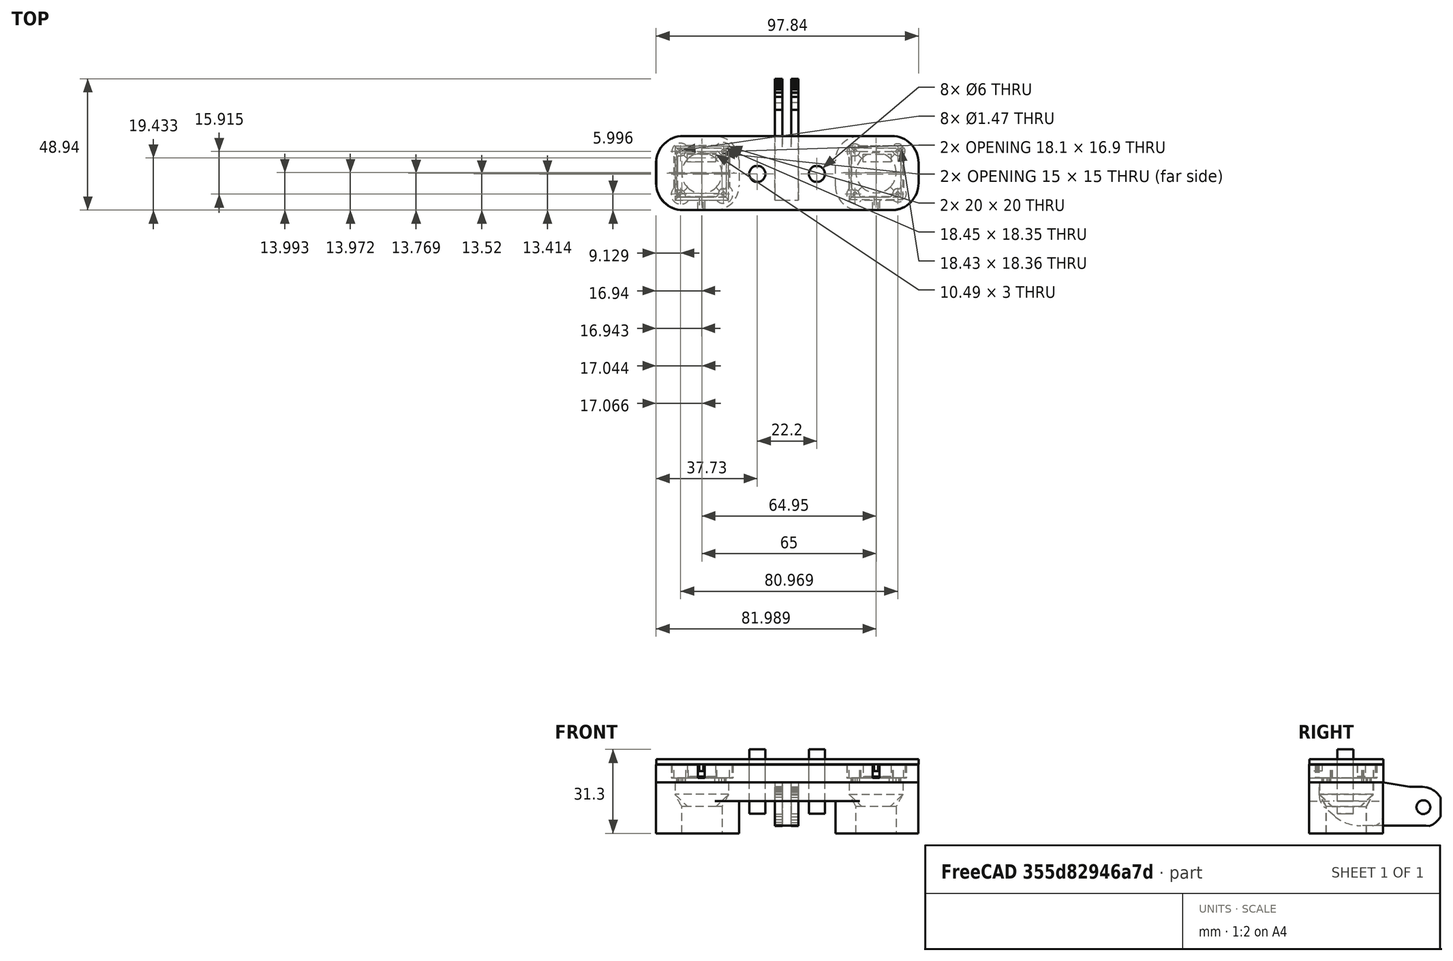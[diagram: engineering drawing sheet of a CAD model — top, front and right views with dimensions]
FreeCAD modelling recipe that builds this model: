
FCSTD DOCUMENT  (FreeCAD 0.19R24267 +99 (Git))
Label: 3D相机支架
License: All rights reserved
LicenseURL: http://en.wikipedia.org/wiki/All_rights_reserved
objects: Sketcher::SketchObject×15, PartDesign::Pad×11, Part::Cylinder×8, PartDesign::Fillet×7, App::Part×7, PartDesign::Body×6, Part::Cut×4, PartDesign::Pocket×3, PartDesign::ShapeBinder×2, Image::ImagePlane×1, PartDesign::Plane×1, PartDesign::AdditiveLoft×1, Mesh::Feature×1, Part::MultiFuse×1, App::MeasureDistance×1
note: 81 computed .brp shape members not serialized (recipe doc carries the construction recipe); baked Part::Feature solids carry a one-line shape summary decoded from their .brp

FEATURE [Image::ImagePlane] ImagePlane
  Placement = pos=(0.0706851,8.99972,0) rot=(0,0,-1;4.72024rad)
  XSize = 131.603
  YSize = 98.9214
FEATURE [Sketcher::SketchObject] Sketch
  FullyConstrained = false
  MapMode = 5
  Support = -> [XY_Plane]
  sketch-geometry (26):
    g0: LineSegment StartX=-2.6098 StartY=9.91969 StartZ=0 EndX=16.3902 EndY=9.91969 EndZ=0
    g1: LineSegment StartX=16.3902 StartY=9.91969 StartZ=0 EndX=16.3902 EndY=-9.08031 EndZ=0
    g2: LineSegment StartX=16.3902 StartY=-9.08031 StartZ=0 EndX=-2.6098 EndY=-9.08031 EndZ=0
    g3: LineSegment StartX=-2.6098 StartY=-9.08031 StartZ=0 EndX=-2.6098 EndY=9.91969 EndZ=0
    g4: Circle CenterX=-1.02434 CenterY=8.30105 CenterZ=0 NormalX=0 NormalY=0 NormalZ=1 AngleXU=0 Radius=0.734567
    g5: Circle CenterX=14.8836 CenterY=8.28387 CenterZ=0 NormalX=0 NormalY=0 NormalZ=1 AngleXU=0 Radius=0.734567
    g6: Circle CenterX=14.891 CenterY=-7.66127 CenterZ=0 NormalX=0 NormalY=0 NormalZ=1 AngleXU=0 Radius=0.734567
    g7: Circle CenterX=-0.958796 CenterY=-7.66815 CenterZ=0 NormalX=0 NormalY=0 NormalZ=1 AngleXU=0 Radius=0.734567
    g8: LineSegment StartX=0.44853 StartY=8.13558 StartZ=0 EndX=0.44853 EndY=8.77965 EndZ=0
    g9: ArcOfCircle CenterX=1.08417 CenterY=8.77965 CenterZ=0 NormalX=0 NormalY=0 NormalZ=1 AngleXU=0 Radius=0.63564 StartAngle=1.66062 EndAngle=3.14159
    g10: LineSegment StartX=1.02715 StartY=9.41273 StartZ=0 EndX=12.8411 EndY=9.41273 EndZ=0
    g11: ArcOfCircle CenterX=12.8411 CenterY=8.9738 CenterZ=0 NormalX=0 NormalY=0 NormalZ=1 AngleXU=0 Radius=0.43893 StartAngle=6.26572 EndAngle=7.85398
    g12: LineSegment StartX=13.2799 StartY=8.96613 StartZ=0 EndX=13.2799 EndY=8.11104 EndZ=0
    g13: ArcOfCircle CenterX=14.9168 CenterY=8.11104 CenterZ=0 NormalX=0 NormalY=0 NormalZ=1 AngleXU=0 Radius=1.63683 StartAngle=3.14159 EndAngle=4.6686
    g14: LineSegment StartX=14.8451 StartY=6.47577 StartZ=0 EndX=14.8451 EndY=-5.31443 EndZ=0
    g15: ArcOfCircle CenterX=14.0301 CenterY=-5.31443 CenterZ=0 NormalX=0 NormalY=0 NormalZ=1 AngleXU=0 Radius=0.815031 StartAngle=5.24992 EndAngle=6.28319
    g16: ArcOfCircle CenterX=15.6798 CenterY=-8.0821 CenterZ=0 NormalX=0 NormalY=0 NormalZ=1 AngleXU=0 Radius=2.40703 StartAngle=2.10833 EndAngle=3.12033
    g17: ArcOfCircle CenterX=12.6009 CenterY=-8.01664 CenterZ=0 NormalX=0 NormalY=0 NormalZ=1 AngleXU=0 Radius=0.67253 StartAngle=4.81773 EndAngle=6.26193
    g18: LineSegment StartX=12.6717 StartY=-8.68544 StartZ=0 EndX=1.5102 EndY=-8.68544 EndZ=0
    g19: ArcOfCircle CenterX=1.5102 CenterY=-8.10037 CenterZ=0 NormalX=0 NormalY=0 NormalZ=1 AngleXU=0 Radius=0.585068 StartAngle=3.0331 EndAngle=4.71239
    g20: LineSegment StartX=0.928577 StartY=-8.03702 StartZ=0 EndX=0.928577 EndY=-7.40934 EndZ=0
    g21: ArcOfCircle CenterX=-0.654332 CenterY=-7.40934 CenterZ=0 NormalX=0 NormalY=0 NormalZ=1 AngleXU=0 Radius=1.58291 StartAngle=0 EndAngle=1.58988
    g22: ArcOfCircle CenterX=-0.710267 CenterY=-4.47836 CenterZ=0 NormalX=0 NormalY=0 NormalZ=1 AngleXU=0 Radius=1.34861 StartAngle=3.18344 EndAngle=4.73147
    g23: LineSegment StartX=-2.0577 StartY=-4.53478 StartZ=0 EndX=-2.0577 EndY=5.76747 EndZ=0
    g24: ArcOfCircle CenterX=-1.11072 CenterY=5.76747 CenterZ=0 NormalX=0 NormalY=0 NormalZ=1 AngleXU=0 Radius=0.94698 StartAngle=1.54594 EndAngle=3.14159
    g25: ArcOfCircle CenterX=-1.0499 CenterY=8.21418 CenterZ=0 NormalX=0 NormalY=0 NormalZ=1 AngleXU=0 Radius=1.50049 StartAngle=4.68754 EndAngle=6.23078
  constraints (35):
    c: Coincident(g0,g1)
    c: Coincident(g1,g2)
    c: Coincident(g2,g3)
    c: Coincident(g3,g0)
    c: Horizontal(g0)
    c: Horizontal(g2)
    c: Vertical(g1)
    c: Vertical(g3)
    c: Distance(g0) = 19
    c: Equal(g3,g0)
    c: Vertical(g8)
    c: Tangent(g8,g9) = 1.5708
    c: Coincident(g9,g10)
    c: Horizontal(g10)
    c: Tangent(g10,g11) = 1.5708
    c: Coincident(g11,g12)
    c: Vertical(g12)
    c: Tangent(g12,g13) = -1.5708
    c: Coincident(g13,g14)
    c: Vertical(g14)
    c: Tangent(g14,g15) = 1.5708
    c: Tangent(g15,g16) = 1.5708
    c: Tangent(g16,g17) = 1.5708
    c: Coincident(g17,g18)
    c: Horizontal(g18)
    c: Tangent(g18,g19) = 1.5708
    c: Coincident(g19,g20)
    c: Vertical(g20)
    c: Tangent(g20,g21) = -1.5708
    c: Tangent(g21,g22) = 1.5708
    c: Coincident(g22,g23)
    c: Vertical(g23)
    c: Tangent(g23,g24) = 1.5708
    c: Tangent(g24,g25) = 1.5708
    c: Coincident(g25,g8)
FEATURE [PartDesign::Pad] Pad
  Direction = (1,1,1)
  Length = 1.6
  Length2 = 100
  Profile = -> Sketch
  Type = 0
FEATURE [PartDesign::Body] Body
  Group = -> [Sketch,Pad]
  Origin = -> Origin
  Placement = pos=(0,0,0) rot=(0,0,1;1.5708rad)
  Tip = -> Pad
FEATURE [Sketcher::SketchObject] Sketch001
  FullyConstrained = false
  MapMode = 5
  Support = -> [XY_Plane001]
  sketch-geometry (26):
    g0: LineSegment StartX=-2.6098 StartY=9.91969 StartZ=0 EndX=16.3902 EndY=9.91969 EndZ=0
    g1: LineSegment StartX=16.3902 StartY=9.91969 StartZ=0 EndX=16.3902 EndY=-9.08031 EndZ=0
    g2: LineSegment StartX=16.3902 StartY=-9.08031 StartZ=0 EndX=-2.6098 EndY=-9.08031 EndZ=0
    g3: LineSegment StartX=-2.6098 StartY=-9.08031 StartZ=0 EndX=-2.6098 EndY=9.91969 EndZ=0
    g4: Circle CenterX=-1.02434 CenterY=8.30105 CenterZ=0 NormalX=0 NormalY=0 NormalZ=1 AngleXU=0 Radius=0.734567
    g5: Circle CenterX=14.8836 CenterY=8.28387 CenterZ=0 NormalX=0 NormalY=0 NormalZ=1 AngleXU=0 Radius=0.734567
    g6: Circle CenterX=14.891 CenterY=-7.66127 CenterZ=0 NormalX=0 NormalY=0 NormalZ=1 AngleXU=0 Radius=0.734567
    g7: Circle CenterX=-0.958796 CenterY=-7.66815 CenterZ=0 NormalX=0 NormalY=0 NormalZ=1 AngleXU=0 Radius=0.734567
    g8: LineSegment StartX=0.44853 StartY=8.13558 StartZ=0 EndX=0.44853 EndY=8.77965 EndZ=0
    g9: ArcOfCircle CenterX=1.08417 CenterY=8.77965 CenterZ=0 NormalX=0 NormalY=0 NormalZ=1 AngleXU=0 Radius=0.63564 StartAngle=1.66062 EndAngle=3.14159
    g10: LineSegment StartX=1.02715 StartY=9.41273 StartZ=0 EndX=12.8411 EndY=9.41273 EndZ=0
    g11: ArcOfCircle CenterX=12.8411 CenterY=8.9738 CenterZ=0 NormalX=0 NormalY=0 NormalZ=1 AngleXU=0 Radius=0.43893 StartAngle=6.26572 EndAngle=7.85398
    g12: LineSegment StartX=13.2799 StartY=8.96613 StartZ=0 EndX=13.2799 EndY=8.11104 EndZ=0
    g13: ArcOfCircle CenterX=14.9168 CenterY=8.11104 CenterZ=0 NormalX=0 NormalY=0 NormalZ=1 AngleXU=0 Radius=1.63683 StartAngle=3.14159 EndAngle=4.6686
    g14: LineSegment StartX=14.8451 StartY=6.47577 StartZ=0 EndX=14.8451 EndY=-5.31443 EndZ=0
    g15: ArcOfCircle CenterX=14.0301 CenterY=-5.31443 CenterZ=0 NormalX=0 NormalY=0 NormalZ=1 AngleXU=0 Radius=0.815031 StartAngle=5.24992 EndAngle=6.28319
    g16: ArcOfCircle CenterX=15.6798 CenterY=-8.0821 CenterZ=0 NormalX=0 NormalY=0 NormalZ=1 AngleXU=0 Radius=2.40703 StartAngle=2.10833 EndAngle=3.12033
    g17: ArcOfCircle CenterX=12.6009 CenterY=-8.01664 CenterZ=0 NormalX=0 NormalY=0 NormalZ=1 AngleXU=0 Radius=0.67253 StartAngle=4.81773 EndAngle=6.26193
    g18: LineSegment StartX=12.6717 StartY=-8.68544 StartZ=0 EndX=1.5102 EndY=-8.68544 EndZ=0
    g19: ArcOfCircle CenterX=1.5102 CenterY=-8.10037 CenterZ=0 NormalX=0 NormalY=0 NormalZ=1 AngleXU=0 Radius=0.585068 StartAngle=3.0331 EndAngle=4.71239
    g20: LineSegment StartX=0.928577 StartY=-8.03702 StartZ=0 EndX=0.928577 EndY=-7.40934 EndZ=0
    g21: ArcOfCircle CenterX=-0.654332 CenterY=-7.40934 CenterZ=0 NormalX=0 NormalY=0 NormalZ=1 AngleXU=0 Radius=1.58291 StartAngle=0 EndAngle=1.58988
    g22: ArcOfCircle CenterX=-0.710267 CenterY=-4.47836 CenterZ=0 NormalX=0 NormalY=0 NormalZ=1 AngleXU=0 Radius=1.34861 StartAngle=3.18344 EndAngle=4.73147
    g23: LineSegment StartX=-2.0577 StartY=-4.53478 StartZ=0 EndX=-2.0577 EndY=5.76747 EndZ=0
    g24: ArcOfCircle CenterX=-1.11072 CenterY=5.76747 CenterZ=0 NormalX=0 NormalY=0 NormalZ=1 AngleXU=0 Radius=0.94698 StartAngle=1.54594 EndAngle=3.14159
    g25: ArcOfCircle CenterX=-1.0499 CenterY=8.21418 CenterZ=0 NormalX=0 NormalY=0 NormalZ=1 AngleXU=0 Radius=1.50049 StartAngle=4.68754 EndAngle=6.23078
  constraints (35):
    c: Coincident(g0,g1)
    c: Coincident(g1,g2)
    c: Coincident(g2,g3)
    c: Coincident(g3,g0)
    c: Horizontal(g0)
    c: Horizontal(g2)
    c: Vertical(g1)
    c: Vertical(g3)
    c: Distance(g0) = 19
    c: Equal(g3,g0)
    c: Vertical(g8)
    c: Tangent(g8,g9) = 1.5708
    c: Coincident(g9,g10)
    c: Horizontal(g10)
    c: Tangent(g10,g11) = 1.5708
    c: Coincident(g11,g12)
    c: Vertical(g12)
    c: Tangent(g12,g13) = -1.5708
    c: Coincident(g13,g14)
    c: Vertical(g14)
    c: Tangent(g14,g15) = 1.5708
    c: Tangent(g15,g16) = 1.5708
    c: Tangent(g16,g17) = 1.5708
    c: Coincident(g17,g18)
    c: Horizontal(g18)
    c: Tangent(g18,g19) = 1.5708
    c: Coincident(g19,g20)
    c: Vertical(g20)
    c: Tangent(g20,g21) = -1.5708
    c: Tangent(g21,g22) = 1.5708
    c: Coincident(g22,g23)
    c: Vertical(g23)
    c: Tangent(g23,g24) = 1.5708
    c: Tangent(g24,g25) = 1.5708
    c: Coincident(g25,g8)
FEATURE [PartDesign::Pad] Pad001
  Direction = (1,1,1)
  Length = 1.6
  Length2 = 100
  Profile = -> Sketch001
  Type = 0
FEATURE [PartDesign::Body] Body001
  Group = -> [Sketch001,Pad001]
  Origin = -> Origin001
  Placement = pos=(65,-1.4e-14,0) rot=(0,0,1;1.5708rad)
  Tip = -> Pad001
FEATURE [Sketcher::SketchObject] Sketch002
  FullyConstrained = false
  MapMode = 5
  Support = -> [XY_Plane002]
  sketch-geometry (12):
    g0: LineSegment StartX=-17.432 StartY=20.571 StartZ=0 EndX=80.3236 EndY=20.571 EndZ=0
    g1: LineSegment StartX=80.3236 StartY=20.571 StartZ=0 EndX=80.3236 EndY=-7.01778 EndZ=0
    g2: LineSegment StartX=80.3236 StartY=-7.01778 StartZ=0 EndX=-17.432 EndY=-7.01778 EndZ=0
    g3: LineSegment StartX=-17.432 StartY=-7.01778 StartZ=0 EndX=-17.432 EndY=20.571 EndZ=0
    g4: LineSegment StartX=-9.71325 StartY=16.1288 StartZ=0 EndX=8.73847 EndY=16.1288 EndZ=0
    g5: LineSegment StartX=8.73847 StartY=16.1288 StartZ=0 EndX=8.73847 EndY=-2.22466 EndZ=0
    g6: LineSegment StartX=8.73847 StartY=-2.22466 StartZ=0 EndX=-9.71325 EndY=-2.22466 EndZ=0
    g7: LineSegment StartX=-9.71325 StartY=-2.22466 StartZ=0 EndX=-9.71325 EndY=16.1288 EndZ=0
    g8: LineSegment StartX=55.3452 StartY=16.1523 StartZ=0 EndX=73.7733 EndY=16.1523 EndZ=0
    g9: LineSegment StartX=73.7733 StartY=16.1523 StartZ=0 EndX=73.7733 EndY=-2.20537 EndZ=0
    g10: LineSegment StartX=73.7733 StartY=-2.20537 StartZ=0 EndX=55.3452 EndY=-2.20537 EndZ=0
    g11: LineSegment StartX=55.3452 StartY=-2.20537 StartZ=0 EndX=55.3452 EndY=16.1523 EndZ=0
  constraints (24):
    c: Coincident(g0,g1)
    c: Coincident(g1,g2)
    c: Coincident(g2,g3)
    c: Coincident(g3,g0)
    c: Horizontal(g0)
    c: Horizontal(g2)
    c: Vertical(g1)
    c: Vertical(g3)
    c: Coincident(g4,g5)
    c: Coincident(g5,g6)
    c: Coincident(g6,g7)
    c: Coincident(g7,g4)
    c: Horizontal(g4)
    c: Horizontal(g6)
    c: Vertical(g5)
    c: Vertical(g7)
    c: Coincident(g8,g9)
    c: Coincident(g9,g10)
    c: Coincident(g10,g11)
    c: Coincident(g11,g8)
    c: Horizontal(g8)
    c: Horizontal(g10)
    c: Vertical(g9)
    c: Vertical(g11)
FEATURE [PartDesign::Pad] Pad002
  Direction = (1,1,1)
  Length = 1.6
  Length2 = 100
  Profile = -> Sketch002
  Type = 0
FEATURE [Sketcher::SketchObject] Sketch003
  ExternalGeometry = -> [Pad002]
  FullyConstrained = false
  MapMode = 5
  Placement = pos=(0,0,1.6) rot=(0,0,1;0rad)
  Support = -> [Pad002]
  sketch-geometry (20):
    g0: ArcOfCircle CenterX=-8.39912 CenterY=14.8619 CenterZ=0 NormalX=0 NormalY=0 NormalZ=1 AngleXU=0 Radius=3.11861 StartAngle=0.810898 EndAngle=3.8862
    g1: LineSegment StartX=-6.25088 StartY=17.1226 StartZ=0 EndX=5.01763 EndY=17.1226 EndZ=0
    g2: ArcOfCircle CenterX=7.48864 CenterY=14.9182 CenterZ=0 NormalX=0 NormalY=0 NormalZ=1 AngleXU=0 Radius=3.31135 StartAngle=5.53813 EndAngle=8.69636
    g3: LineSegment StartX=9.92265 StartY=12.6731 StartZ=0 EndX=9.92265 EndY=1.73188 EndZ=0
    g4: ArcOfCircle CenterX=7.71 CenterY=-0.982007 CenterZ=0 NormalX=0 NormalY=0 NormalZ=1 AngleXU=0 Radius=3.50157 StartAngle=3.92905 EndAngle=7.16998
    g5: LineSegment StartX=5.23912 StartY=-3.46308 StartZ=0 EndX=-5.40416 EndY=-3.46308 EndZ=0
    g6: ArcOfCircle CenterX=-8.20355 CenterY=-1.21839 CenterZ=0 NormalX=0 NormalY=0 NormalZ=1 AngleXU=0 Radius=3.58821 StartAngle=2.33729 EndAngle=5.60732
    g7: LineSegment StartX=-10.6924 StartY=1.36635 StartZ=0 EndX=-10.6924 EndY=12.7484 EndZ=0
    g8: ArcOfCircle CenterX=56.645 CenterY=14.753 CenterZ=0 NormalX=0 NormalY=0 NormalZ=1 AngleXU=0 Radius=2.88595 StartAngle=0.890269 EndAngle=3.86492
    g9: LineSegment StartX=58.4608 StartY=16.9961 StartZ=0 EndX=70.8307 EndY=16.9961 EndZ=0
    g10: ArcOfCircle CenterX=72.6637 CenterY=15.0338 CenterZ=0 NormalX=0 NormalY=0 NormalZ=1 AngleXU=0 Radius=2.68524 StartAngle=5.63874 EndAngle=8.60532
    g11: LineSegment StartX=74.8104 StartY=13.4206 StartZ=0 EndX=74.8104 EndY=1.34255 EndZ=0
    g12: ArcOfCircle CenterX=72.8298 CenterY=-0.933697 CenterZ=0 NormalX=0 NormalY=0 NormalZ=1 AngleXU=0 Radius=3.01727 StartAngle=4.08071 EndAngle=7.13793
    g13: LineSegment StartX=71.0481 StartY=-3.36875 StartZ=0 EndX=59.032 EndY=-3.36875 EndZ=0
    g14: ArcOfCircle CenterX=56.7248 CenterY=-1.25151 CenterZ=0 NormalX=0 NormalY=0 NormalZ=1 AngleXU=0 Radius=3.13143 StartAngle=2.36935 EndAngle=5.54069
    g15: LineSegment StartX=54.4816 StartY=0.933413 StartZ=0 EndX=54.4816 EndY=12.8429 EndZ=0
    g16: LineSegment StartX=-17.432 StartY=20.571 StartZ=0 EndX=80.3236 EndY=20.571 EndZ=0
    g17: LineSegment StartX=80.3236 StartY=20.571 StartZ=0 EndX=80.3236 EndY=-7.01778 EndZ=0
    g18: LineSegment StartX=80.3236 StartY=-7.01778 StartZ=0 EndX=-17.432 EndY=-7.01778 EndZ=0
    g19: LineSegment StartX=-17.432 StartY=-7.01778 StartZ=0 EndX=-17.432 EndY=20.571 EndZ=0
  constraints (34):
    c: Coincident(g0,g1)
    c: Horizontal(g1)
    c: Coincident(g2,g3)
    c: Coincident(g4,g5)
    c: Horizontal(g5)
    c: Coincident(g6,g7)
    c: Vertical(g7)
    c: Coincident(g7,g0)
    c: Coincident(g2,g1)
    c: Vertical(g3)
    c: Coincident(g4,g3)
    c: Coincident(g5,g6)
    c: Coincident(g8,g9)
    c: Horizontal(g9)
    c: Coincident(g10,g11)
    c: Coincident(g12,g13)
    c: Horizontal(g13)
    c: Coincident(g14,g15)
    c: Vertical(g15)
    c: Coincident(g15,g8)
    c: Coincident(g10,g9)
    c: Vertical(g11)
    c: Coincident(g12,g11)
    c: Coincident(g13,g14)
    c: Coincident(g16,g17)
    c: Coincident(g17,g18)
    c: Coincident(g18,g19)
    c: Coincident(g19,g16)
    c: Horizontal(g16)
    c: Horizontal(g18)
    c: Vertical(g17)
    c: Vertical(g19)
    c: Coincident(g16,g-5)
    c: Coincident(g17,g-6)
FEATURE [PartDesign::Pad] Pad003
  BaseFeature = -> Pad002
  Direction = (1,1,1)
  Length = 5
  Length2 = 100
  Profile = -> Sketch003
  Type = 0
FEATURE [PartDesign::ShapeBinder] CopyPad003
  TraceSupport = false
FEATURE [Sketcher::SketchObject] Sketch004
  FullyConstrained = false
  MapMode = 5
  Placement = pos=(0,0,0) rot=(1,0,0;3.14159rad)
  Support = -> [CopyPad003]
  sketch-geometry (12):
    g0: LineSegment StartX=-10.3859 StartY=3.2507 StartZ=0 EndX=9.61406 EndY=3.2507 EndZ=0
    g1: LineSegment StartX=9.61406 StartY=3.2507 StartZ=0 EndX=9.61406 EndY=-16.7493 EndZ=0
    g2: LineSegment StartX=9.61406 StartY=-16.7493 StartZ=0 EndX=-10.3859 EndY=-16.7493 EndZ=0
    g3: LineSegment StartX=-10.3859 StartY=-16.7493 StartZ=0 EndX=-10.3859 EndY=3.2507 EndZ=0
    g4: LineSegment StartX=74.5643 StartY=3.08146 StartZ=0 EndX=74.5643 EndY=-16.9185 EndZ=0
    g5: LineSegment StartX=54.5643 StartY=3.08146 StartZ=0 EndX=74.5643 EndY=3.08146 EndZ=0
    g6: LineSegment StartX=74.5643 StartY=-16.9185 StartZ=0 EndX=54.5643 EndY=-16.9185 EndZ=0
    g7: LineSegment StartX=54.5643 StartY=-16.9185 StartZ=0 EndX=54.5643 EndY=3.08146 EndZ=0
    g8: LineSegment StartX=-17.4318 StartY=7.01779 StartZ=0 EndX=80.319 EndY=7.01779 EndZ=0
    g9: LineSegment StartX=80.319 StartY=7.01779 StartZ=0 EndX=80.319 EndY=-20.5415 EndZ=0
    g10: LineSegment StartX=80.319 StartY=-20.5415 StartZ=0 EndX=-17.4318 EndY=-20.5415 EndZ=0
    g11: LineSegment StartX=-17.4318 StartY=-20.5415 StartZ=0 EndX=-17.4318 EndY=7.01779 EndZ=0
  constraints (28):
    c: Coincident(g0,g1)
    c: Coincident(g1,g2)
    c: Coincident(g2,g3)
    c: Coincident(g3,g0)
    c: Horizontal(g0)
    c: Horizontal(g2)
    c: Vertical(g1)
    c: Vertical(g3)
    c: Equal(g0,g3)
    c: Distance(g0) = 20
    c: Coincident(g5,g4)
    c: Coincident(g4,g6)
    c: Coincident(g6,g7)
    c: Coincident(g7,g5)
    c: Horizontal(g5)
    c: Horizontal(g6)
    c: Vertical(g4)
    c: Vertical(g7)
    c: Equal(g5,g7)
    c: Equal(g0,g5) = 20
    c: Coincident(g8,g9)
    c: Coincident(g9,g10)
    c: Coincident(g10,g11)
    c: Coincident(g11,g8)
    c: Horizontal(g8)
    c: Horizontal(g10)
    c: Vertical(g9)
    c: Vertical(g11)
FEATURE [PartDesign::Pad] Pad004
  Direction = (1,1,1)
  Length = 4.5
  Length2 = 100
  Profile = -> Sketch004
  Type = 0
FEATURE [Sketcher::SketchObject] Sketch005
  ExternalGeometry = -> [Pad004]
  FullyConstrained = true
  MapMode = 5
  Placement = pos=(0,0,-4.5) rot=(1,0,0;3.14159rad)
  Support = -> [Pad004]
  sketch-geometry (12):
    g0: LineSegment StartX=-17.4318 StartY=7.01779 StartZ=0 EndX=80.319 EndY=7.01779 EndZ=0
    g1: LineSegment StartX=80.319 StartY=7.01779 StartZ=0 EndX=80.319 EndY=-20.5415 EndZ=0
    g2: LineSegment StartX=80.319 StartY=-20.5415 StartZ=0 EndX=-17.4318 EndY=-20.5415 EndZ=0
    g3: LineSegment StartX=-17.4318 StartY=-20.5415 StartZ=0 EndX=-17.4318 EndY=7.01779 EndZ=0
    g4: LineSegment StartX=-10.3859 StartY=3.2507 StartZ=0 EndX=9.61406 EndY=3.2507 EndZ=0
    g5: LineSegment StartX=9.61406 StartY=3.2507 StartZ=0 EndX=9.61406 EndY=-16.7493 EndZ=0
    g6: LineSegment StartX=9.61406 StartY=-16.7493 StartZ=0 EndX=-10.3859 EndY=-16.7493 EndZ=0
    g7: LineSegment StartX=-10.3859 StartY=-16.7493 StartZ=0 EndX=-10.3859 EndY=3.2507 EndZ=0
    g8: LineSegment StartX=54.5643 StartY=3.08146 StartZ=0 EndX=74.5643 EndY=3.08146 EndZ=0
    g9: LineSegment StartX=74.5643 StartY=3.08146 StartZ=0 EndX=74.5643 EndY=-16.9185 EndZ=0
    g10: LineSegment StartX=74.5643 StartY=-16.9185 StartZ=0 EndX=54.5643 EndY=-16.9185 EndZ=0
    g11: LineSegment StartX=54.5643 StartY=-16.9185 StartZ=0 EndX=54.5643 EndY=3.08146 EndZ=0
  constraints (30):
    c: Coincident(g0,g1)
    c: Coincident(g1,g2)
    c: Coincident(g2,g3)
    c: Coincident(g3,g0)
    c: Horizontal(g0)
    c: Horizontal(g2)
    c: Vertical(g1)
    c: Vertical(g3)
    c: Coincident(g0,g-3)
    c: Coincident(g1,g-4)
    c: Coincident(g4,g5)
    c: Coincident(g5,g6)
    c: Coincident(g6,g7)
    c: Coincident(g7,g4)
    c: Horizontal(g4)
    c: Horizontal(g6)
    c: Vertical(g5)
    c: Vertical(g7)
    c: Coincident(g4,g-8)
    c: Coincident(g5,g-5)
    c: Coincident(g8,g9)
    c: Coincident(g9,g10)
    c: Coincident(g10,g11)
    c: Coincident(g11,g8)
    c: Horizontal(g8)
    c: Horizontal(g10)
    c: Vertical(g9)
    c: Vertical(g11)
    c: Coincident(g8,g-6)
    c: Coincident(g9,g-7)
FEATURE [PartDesign::ShapeBinder] CopyXY_Plane004
  TraceSupport = false
FEATURE [PartDesign::Plane] DatumPlane
  AttachmentOffset = pos=(0,0,-9) rot=(0,0,1;0rad)
  Length = 119.832
  MapMode = 5
  Placement = pos=(0,0,-9) rot=(0,0,1;0rad)
  ResizeMode = 0
  Support = -> [CopyXY_Plane004]
  Width = 64.5134
FEATURE [Sketcher::SketchObject] Sketch006
  ExternalGeometry = -> [Sketch005]
  FullyConstrained = true
  MapMode = 5
  Placement = pos=(0,0,-9) rot=(0,0,1;0rad)
  Support = -> [DatumPlane]
  sketch-geometry (12):
    g0: LineSegment StartX=-17.4318 StartY=20.5415 StartZ=0 EndX=80.319 EndY=20.5415 EndZ=0
    g1: LineSegment StartX=80.319 StartY=20.5415 StartZ=0 EndX=80.319 EndY=-7.01779 EndZ=0
    g2: LineSegment StartX=80.319 StartY=-7.01779 StartZ=0 EndX=-17.4318 EndY=-7.01779 EndZ=0
    g3: LineSegment StartX=-17.4318 StartY=-7.01779 StartZ=0 EndX=-17.4318 EndY=20.5415 EndZ=0
    g4: LineSegment StartX=-10.3859 StartY=16.7493 StartZ=0 EndX=9.61406 EndY=-3.2507 EndZ=0
    g5: LineSegment StartX=9.61406 StartY=16.7493 StartZ=0 EndX=-10.3859 EndY=-3.2507 EndZ=0
    g6: GeomPoint X=-0.385936 Y=6.7493 Z=0
    g7: LineSegment StartX=54.5643 StartY=16.9185 StartZ=0 EndX=74.5643 EndY=-3.08146 EndZ=0
    g8: LineSegment StartX=74.5643 StartY=16.9185 StartZ=0 EndX=54.5643 EndY=-3.08146 EndZ=0
    g9: GeomPoint X=64.5643 Y=6.91854 Z=0
    g10: Circle CenterX=-0.385936 CenterY=6.7493 CenterZ=0 NormalX=0 NormalY=0 NormalZ=1 AngleXU=0 Radius=7.5
    g11: Circle CenterX=64.5643 CenterY=6.91854 CenterZ=0 NormalX=0 NormalY=0 NormalZ=1 AngleXU=0 Radius=7.5
  constraints (26):
    c: Coincident(g0,g1)
    c: Coincident(g1,g2)
    c: Coincident(g2,g3)
    c: Coincident(g3,g0)
    c: Horizontal(g0)
    c: Horizontal(g2)
    c: Vertical(g1)
    c: Vertical(g3)
    c: Coincident(g-7,g0)
    c: Coincident(g1,g-8)
    c: Coincident(g4,g-3)
    c: Coincident(g4,g-5)
    c: Coincident(g5,g-3)
    c: Coincident(g5,g-5)
    c: PointOnObject(g6,g5)
    c: PointOnObject(g6,g4)
    c: Coincident(g7,g-4)
    c: Coincident(g7,g-6)
    c: Coincident(g8,g-4)
    c: Coincident(g8,g-6)
    c: PointOnObject(g9,g8)
    c: PointOnObject(g9,g7)
    c: Coincident(g10,g6)
    c: Diameter(g10) = 15
    c: Coincident(g11,g9)
    c: Diameter(g11) = 15
FEATURE [PartDesign::AdditiveLoft] AdditiveLoft
  BaseFeature = -> Pad004
  Closed = false
  Profile = -> Sketch005
  Ruled = false
  Sections = -> [Sketch006]
FEATURE [PartDesign::Pad] Pad005
  BaseFeature = -> AdditiveLoft
  Direction = (1,1,1)
  Length = 10
  Length2 = 100
  Profile = -> AdditiveLoft [Face17]
  Type = 0
FEATURE [PartDesign::Fillet] Fillet
  Base = -> Pad005 [Edge50,Edge47,Edge46,Edge52]
  BaseFeature = -> Pad005
  Radius = 10
  SupportTransform = false
FEATURE [Sketcher::SketchObject] Sketch007
  ExternalGeometry = -> [Fillet]
  FullyConstrained = false
  MapMode = 5
  Placement = pos=(0,0,-19) rot=(1,0,0;3.14159rad)
  Support = -> [Fillet]
  sketch-geometry (6):
    g0: LineSegment StartX=13.4592 StartY=8.86174 StartZ=0 EndX=49.428 EndY=8.86174 EndZ=0
    g1: LineSegment StartX=49.428 StartY=8.86174 StartZ=0 EndX=49.428 EndY=-27.2773 EndZ=0
    g2: LineSegment StartX=49.428 StartY=-27.2773 StartZ=0 EndX=13.4592 EndY=-27.2773 EndZ=0
    g3: LineSegment StartX=13.4592 StartY=-27.2773 StartZ=0 EndX=13.4592 EndY=8.86174 EndZ=0
    g4: LineSegment StartX=-17.4318 StartY=-2.98221 StartZ=0 EndX=13.4592 EndY=-2.98221 EndZ=0
    g5: LineSegment StartX=49.428 StartY=-2.98221 StartZ=0 EndX=80.319 EndY=-2.98221 EndZ=0
  constraints (15):
    c: Coincident(g0,g1)
    c: Coincident(g1,g2)
    c: Coincident(g2,g3)
    c: Coincident(g3,g0)
    c: Horizontal(g0)
    c: Horizontal(g2)
    c: Vertical(g1)
    c: Vertical(g3)
    c: Coincident(g4,g-3)
    c: PointOnObject(g4,g3)
    c: Horizontal(g4)
    c: PointOnObject(g5,g1)
    c: Coincident(g5,g-4)
    c: Horizontal(g5)
    c: Equal(g4,g5)
FEATURE [PartDesign::Pocket] Pocket
  BaseFeature = -> Fillet
  Length = 12
  Length2 = 100
  Profile = -> Sketch007
  Type = 0
FEATURE [PartDesign::Fillet] Fillet001
  Base = -> Pocket [Edge72,Edge68,Edge64,Edge74]
  BaseFeature = -> Pocket
  Radius = 9
  SupportTransform = false
FEATURE [PartDesign::Body] Body003
  Group = -> [CopyPad003,Sketch004,Pad004,Sketch005,DatumPlane,CopyXY_Plane004,Sketch006,AdditiveLoft,Pad005,Fillet,Sketch007,Pocket,Fillet001]
  Origin = -> Origin005
  Tip = -> Fillet001
FEATURE [App::Part] Part001  label="相机前框"
  Group = -> [Body003]
  Origin = -> Origin004
FEATURE [PartDesign::Fillet] Fillet002
  Base = -> Pad003 [Edge21,Edge26,Edge24,Edge20]
  BaseFeature = -> Pad003
  Radius = 10
  SupportTransform = false
FEATURE [Sketcher::SketchObject] Sketch008
  FullyConstrained = false
  MapMode = 5
  Placement = pos=(0,0,6.6) rot=(0,0,1;0rad)
  Support = -> [Fillet002]
  sketch-geometry (8):
    g0: LineSegment StartX=-1.83309 StartY=0.606132 StartZ=0 EndX=0.666909 EndY=0.606132 EndZ=0
    g1: LineSegment StartX=0.666909 StartY=0.606132 StartZ=0 EndX=0.666909 EndY=-8.63685 EndZ=0
    g2: LineSegment StartX=0.666909 StartY=-8.63685 StartZ=0 EndX=-1.83309 EndY=-8.63685 EndZ=0
    g3: LineSegment StartX=-1.83309 StartY=-8.63685 StartZ=0 EndX=-1.83309 EndY=0.606132 EndZ=0
    g4: LineSegment StartX=63.2717 StartY=0.846198 StartZ=0 EndX=65.7717 EndY=0.846198 EndZ=0
    g5: LineSegment StartX=65.7717 StartY=0.846198 StartZ=0 EndX=65.7717 EndY=-9.55029 EndZ=0
    g6: LineSegment StartX=65.7717 StartY=-9.55029 StartZ=0 EndX=63.2717 EndY=-9.55029 EndZ=0
    g7: LineSegment StartX=63.2717 StartY=-9.55029 StartZ=0 EndX=63.2717 EndY=0.846198 EndZ=0
  constraints (18):
    c: Coincident(g0,g1)
    c: Coincident(g1,g2)
    c: Coincident(g2,g3)
    c: Coincident(g3,g0)
    c: Horizontal(g0)
    c: Horizontal(g2)
    c: Vertical(g1)
    c: Vertical(g3)
    c: Distance(g2) = 2.5
    c: Coincident(g4,g5)
    c: Coincident(g5,g6)
    c: Coincident(g6,g7)
    c: Coincident(g7,g4)
    c: Horizontal(g4)
    c: Horizontal(g6)
    c: Vertical(g5)
    c: Vertical(g7)
    c: Equal(g2,g6) = 2.5
FEATURE [PartDesign::Pocket] Pocket001
  BaseFeature = -> Fillet002
  Length = 5
  Length2 = 100
  Profile = -> Sketch008
  Type = 0
FEATURE [PartDesign::Body] Body002
  Group = -> [Sketch002,Pad002,Sketch003,Pad003,Fillet002,Sketch008,Pocket001]
  Origin = -> Origin002
  Tip = -> Pocket001
FEATURE [App::Part] Part  label="相机中框"
  Group = -> [Body,Body001,Body002]
  Origin = -> Origin003
FEATURE [Sketcher::SketchObject] Sketch009
  FullyConstrained = false
  MapMode = 5
  Support = -> [XY_Plane007]
  sketch-geometry (4):
    g0: LineSegment StartX=-17.3659 StartY=20.6304 StartZ=0 EndX=80.4073 EndY=20.6304 EndZ=0
    g1: LineSegment StartX=80.4073 StartY=20.6304 StartZ=0 EndX=80.4073 EndY=-6.97724 EndZ=0
    g2: LineSegment StartX=80.4073 StartY=-6.97724 StartZ=0 EndX=-17.3659 EndY=-6.97724 EndZ=0
    g3: LineSegment StartX=-17.3659 StartY=-6.97724 StartZ=0 EndX=-17.3659 EndY=20.6304 EndZ=0
  constraints (8):
    c: Coincident(g0,g1)
    c: Coincident(g1,g2)
    c: Coincident(g2,g3)
    c: Coincident(g3,g0)
    c: Horizontal(g0)
    c: Horizontal(g2)
    c: Vertical(g1)
    c: Vertical(g3)
FEATURE [PartDesign::Pad] Pad006
  Direction = (1,1,1)
  Length = 2
  Length2 = 100
  Profile = -> Sketch009
  Type = 0
FEATURE [PartDesign::Fillet] Fillet003
  Base = -> Pad006 [Edge8,Edge5,Edge2,Edge1]
  BaseFeature = -> Pad006
  Radius = 10
  SupportTransform = false
FEATURE [Sketcher::SketchObject] Sketch010
  FullyConstrained = false
  MapMode = 5
  Placement = pos=(0,0,0) rot=(1,0,0;3.14159rad)
  Support = -> [Fillet003]
  sketch-geometry (8):
    g0: LineSegment StartX=-1.31726 StartY=6.9529 StartZ=0 EndX=0.182735 EndY=6.9529 EndZ=0
    g1: LineSegment StartX=0.182735 StartY=6.9529 StartZ=0 EndX=0.182735 EndY=2.23283 EndZ=0
    g2: LineSegment StartX=0.182735 StartY=2.23283 StartZ=0 EndX=-1.31726 EndY=2.23283 EndZ=0
    g3: LineSegment StartX=-1.31726 StartY=2.23283 StartZ=0 EndX=-1.31726 EndY=6.9529 EndZ=0
    g4: LineSegment StartX=63.8003 StartY=7.0089 StartZ=0 EndX=65.3003 EndY=7.0089 EndZ=0
    g5: LineSegment StartX=65.3003 StartY=7.0089 StartZ=0 EndX=65.3003 EndY=2.23129 EndZ=0
    g6: LineSegment StartX=65.3003 StartY=2.23129 StartZ=0 EndX=63.8003 EndY=2.23129 EndZ=0
    g7: LineSegment StartX=63.8003 StartY=2.23129 StartZ=0 EndX=63.8003 EndY=7.0089 EndZ=0
  constraints (18):
    c: Coincident(g0,g1)
    c: Coincident(g1,g2)
    c: Coincident(g2,g3)
    c: Coincident(g3,g0)
    c: Horizontal(g0)
    c: Horizontal(g2)
    c: Vertical(g1)
    c: Vertical(g3)
    c: Coincident(g4,g5)
    c: Coincident(g5,g6)
    c: Coincident(g6,g7)
    c: Coincident(g7,g4)
    c: Horizontal(g4)
    c: Horizontal(g6)
    c: Vertical(g5)
    c: Vertical(g7)
    c: Distance(g0) = 1.5
    c: Distance(g4) = 1.5
FEATURE [PartDesign::Pad] Pad007
  BaseFeature = -> Fillet003
  Direction = (1,1,1)
  Length = 2.5
  Length2 = 100
  Profile = -> Sketch010
  Type = 0
FEATURE [Sketcher::SketchObject] Sketch011
  FullyConstrained = false
  MapMode = 5
  Placement = pos=(0,0,0) rot=(1,0,0;3.14159rad)
  Support = -> [Pad007]
  sketch-geometry (16):
    g0: LineSegment StartX=4.75342 StartY=-10.9127 StartZ=0 EndX=-5.73414 EndY=-10.9127 EndZ=0
    g1: LineSegment StartX=-5.73414 StartY=-10.9127 StartZ=0 EndX=-5.73414 EndY=-13.9127 EndZ=0
    g2: LineSegment StartX=-5.73414 StartY=-13.9127 StartZ=0 EndX=4.75342 EndY=-13.9127 EndZ=0
    g3: LineSegment StartX=4.75342 StartY=-13.9127 StartZ=0 EndX=4.75342 EndY=-10.9127 EndZ=0
    g4: LineSegment StartX=-5.73414 StartY=-10.9127 StartZ=0 EndX=4.75342 EndY=-12.4127 EndZ=0
    g5: LineSegment StartX=4.75342 StartY=-12.4127 StartZ=0 EndX=-5.73414 EndY=-13.9127 EndZ=0
    g6: GeomPoint X=4.75342 Y=-16.4127 Z=0
    g7: LineSegment StartX=4.75342 StartY=-12.4127 StartZ=0 EndX=4.75342 EndY=-16.4127 EndZ=0
    g8: LineSegment StartX=70.1062 StartY=-10.924 StartZ=0 EndX=59.7135 EndY=-10.924 EndZ=0
    g9: LineSegment StartX=59.7135 StartY=-10.924 StartZ=0 EndX=59.7135 EndY=-13.924 EndZ=0
    g10: LineSegment StartX=59.7135 StartY=-13.924 StartZ=0 EndX=70.1062 EndY=-13.924 EndZ=0
    g11: LineSegment StartX=70.1062 StartY=-13.924 StartZ=0 EndX=70.1062 EndY=-10.924 EndZ=0
    g12: LineSegment StartX=59.7135 StartY=-10.924 StartZ=0 EndX=70.1062 EndY=-12.424 EndZ=0
    g13: LineSegment StartX=70.1062 StartY=-12.424 StartZ=0 EndX=59.7135 EndY=-13.924 EndZ=0
    g14: GeomPoint X=70.1062 Y=-16.424 Z=0
    g15: LineSegment StartX=70.1062 StartY=-12.424 StartZ=0 EndX=70.1062 EndY=-16.424 EndZ=0
  constraints (36):
    c: Coincident(g0,g1)
    c: Coincident(g1,g2)
    c: Coincident(g2,g3)
    c: Coincident(g3,g0)
    c: Horizontal(g0)
    c: Horizontal(g2)
    c: Vertical(g1)
    c: Vertical(g3)
    c: Distance(g1) = 3
    c: Coincident(g0,g4)
    c: Coincident(g5,g4)
    c: PointOnObject(g4,g3)
    c: Equal(g4,g5)
    c: Coincident(g5,g1)
    c: Coincident(g7,g4)
    c: Coincident(g7,g6)
    c: Vertical(g7)
    c: Distance(g7) = 4
    c: Coincident(g8,g9)
    c: Coincident(g9,g10)
    c: Coincident(g10,g11)
    c: Coincident(g11,g8)
    c: Horizontal(g8)
    c: Horizontal(g10)
    c: Vertical(g9)
    c: Vertical(g11)
    c: Equal(g1,g9) = 3
    c: Coincident(g8,g12)
    c: Coincident(g13,g12)
    c: PointOnObject(g12,g11)
    c: Equal(g12,g13)
    c: Coincident(g13,g9)
    c: Coincident(g15,g12)
    c: Coincident(g15,g14)
    c: Vertical(g15)
    c: Equal(g7,g15) = 4
FEATURE [PartDesign::Pad] Pad008
  BaseFeature = -> Pad007
  Direction = (1,1,1)
  Length = 4.5
  Length2 = 100
  Profile = -> Sketch011
  Type = 0
FEATURE [PartDesign::Body] Body004
  Group = -> [Sketch009,Pad006,Fillet003,Sketch010,Pad007,Sketch011,Pad008]
  Origin = -> Origin007
  Placement = pos=(0,0,6.7) rot=(0,0,1;0rad)
  Tip = -> Pad008
FEATURE [App::Part] Part002  label="相机后盖"
  Group = -> [Body004]
  Origin = -> Origin006
FEATURE [Part::Cylinder] Cylinder  label="圆柱体"
  Angle = 360
  AttacherType = Attacher::AttachEngine3D
  Height = 24
  Placement = pos=(20.3,6.5,-11.7) rot=(0,0,1;0rad)
  Radius = 3
FEATURE [Part::Cylinder] Cylinder001  label="圆柱体001"
  Angle = 360
  AttacherType = Attacher::AttachEngine3D
  Height = 24
  Placement = pos=(42.5,6.5,-11.7) rot=(0,0,1;0rad)
  Radius = 3
FEATURE [App::Part] Part003
  Group = -> [Cylinder,Cylinder001]
  Origin = -> Origin008
FEATURE [Part::Cylinder] Cylinder002  label="圆柱体002"
  Angle = 360
  AttacherType = Attacher::AttachEngine3D
  Height = 24
  Placement = pos=(20.3,6.5,-11.7) rot=(0,0,1;0rad)
  Radius = 3
FEATURE [Part::Cylinder] Cylinder003  label="圆柱体003"
  Angle = 360
  AttacherType = Attacher::AttachEngine3D
  Height = 24
  Placement = pos=(42.5,6.5,-11.7) rot=(0,0,1;0rad)
  Radius = 3
FEATURE [App::Part] Part004
  Group = -> [Cylinder002,Cylinder003]
  Origin = -> Origin009
FEATURE [Part::Cylinder] Cylinder004  label="圆柱体004"
  Angle = 360
  AttacherType = Attacher::AttachEngine3D
  Height = 24
  Placement = pos=(42.5,6.5,-11.7) rot=(0,0,1;0rad)
  Radius = 3
FEATURE [Part::Cylinder] Cylinder005  label="圆柱体005"
  Angle = 360
  AttacherType = Attacher::AttachEngine3D
  Height = 24
  Placement = pos=(20.3,6.5,-11.7) rot=(0,0,1;0rad)
  Radius = 3
FEATURE [App::Part] Part005
  Group = -> [Cylinder005,Cylinder004]
  Origin = -> Origin010
FEATURE [Part::Cut] Cut
  Base = -> Part
  Tool = -> Part003
FEATURE [Part::Cut] Cut001
  Base = -> Part001
  Tool = -> Part004
FEATURE [Part::Cut] Cut002
  Base = -> Part002
  Tool = -> Part005
FEATURE [Mesh::Feature] O3____Body  label="O3头-Body"
  Placement = pos=(21.2,-8.4e-15,-16.5) rot=(-0.57735,-0.57735,-0.57735;2.0944rad)
FEATURE [Sketcher::SketchObject] Sketch013
  AttachmentOffset = pos=(0,0,2.7) rot=(0,0,1;0rad)
  FullyConstrained = false
  MapMode = 5
  Placement = pos=(2.7,-6e-16,6e-16) rot=(0.57735,0.57735,0.57735;2.0944rad)
  Support = -> [YZ_Plane011]
  sketch-geometry (23):
    g0: LineSegment StartX=20.516 StartY=-0.037444 StartZ=0 EndX=30.3661 EndY=-1.64904 EndZ=0
    g1: LineSegment StartX=30.3661 StartY=-1.64904 StartZ=0 EndX=35.2134 EndY=-1.64904 EndZ=0
    g2: LineSegment StartX=35.2134 StartY=-1.64904 StartZ=0 EndX=36.8371 EndY=-1.95946 EndZ=0
    g3: LineSegment StartX=36.8371 StartY=-1.95946 StartZ=0 EndX=38.0071 EndY=-2.29375 EndZ=0
    g4: LineSegment StartX=38.0071 StartY=-2.29375 StartZ=0 EndX=38.3892 EndY=-2.41314 EndZ=0
    g5: LineSegment StartX=38.3892 StartY=-2.41314 StartZ=0 EndX=39.1771 EndY=-2.86682 EndZ=0
    g6: LineSegment StartX=39.1771 StartY=-2.86682 StartZ=0 EndX=39.7263 EndY=-3.22499 EndZ=0
    g7: LineSegment StartX=39.7263 StartY=-3.22499 StartZ=0 EndX=40.2755 EndY=-3.63092 EndZ=0
    g8: LineSegment StartX=40.2755 StartY=-3.63092 StartZ=0 EndX=40.968 EndY=-4.2995 EndZ=0
    g9: LineSegment StartX=40.968 StartY=-4.2995 StartZ=0 EndX=41.2545 EndY=-4.72931 EndZ=0
    g10: LineSegment StartX=41.2545 StartY=-4.72931 StartZ=0 EndX=41.9231 EndY=-5.63668 EndZ=0
    g11: LineSegment StartX=41.9231 StartY=-5.63668 StartZ=0 EndX=41.9231 EndY=-12.8693 EndZ=0
    g12: LineSegment StartX=41.9231 StartY=-12.8693 StartZ=0 EndX=41.062 EndY=-14.0155 EndZ=0
    g13: LineSegment StartX=41.062 StartY=-14.0155 StartZ=0 EndX=40.0353 EndY=-14.9228 EndZ=0
    g14: LineSegment StartX=40.0353 StartY=-14.9228 StartZ=0 EndX=39.0324 EndY=-15.7108 EndZ=0
    g15: LineSegment StartX=39.0324 StartY=-15.7108 StartZ=0 EndX=37.8385 EndY=-16.2361 EndZ=0
    g16: LineSegment StartX=37.8385 StartY=-16.2361 StartZ=0 EndX=36.5252 EndY=-16.1338 EndZ=0
    g17: LineSegment StartX=36.5252 StartY=-16.1338 StartZ=0 EndX=35.1403 EndY=-16.1338 EndZ=0
    g18: LineSegment StartX=35.1403 StartY=-16.1338 StartZ=0 EndX=6.59316 EndY=-16.1338 EndZ=0
    g19: LineSegment StartX=6.59316 StartY=-16.1338 StartZ=0 EndX=-3.28329 EndY=-7.56256 EndZ=0
    g20: LineSegment StartX=-3.28329 StartY=-7.56256 StartZ=0 EndX=-3.28329 EndY=-0.110564 EndZ=0
    g21: LineSegment StartX=-3.28329 StartY=-0.110564 StartZ=0 EndX=20.516 EndY=-0.037444 EndZ=0
    g22: Circle CenterX=35.5519 CenterY=-9.23625 CenterZ=0 NormalX=0 NormalY=0 NormalZ=1 AngleXU=0 Radius=2.56849
  constraints (27):
    c: Coincident(g0,g1)
    c: Horizontal(g1)
    c: Coincident(g1,g2)
    c: Coincident(g2,g3)
    c: Coincident(g3,g4)
    c: Coincident(g4,g5)
    c: Coincident(g5,g6)
    c: Coincident(g6,g7)
    c: Coincident(g7,g8)
    c: Coincident(g8,g9)
    c: Coincident(g9,g10)
    c: Coincident(g10,g11)
    c: Vertical(g11)
    c: Coincident(g11,g12)
    c: Coincident(g12,g13)
    c: Coincident(g13,g14)
    c: Coincident(g14,g15)
    c: Coincident(g15,g16)
    c: Coincident(g16,g17)
    c: Horizontal(g17)
    c: Coincident(g17,g18)
    c: Horizontal(g18)
    c: Coincident(g18,g19)
    c: Coincident(g19,g20)
    c: Vertical(g20)
    c: Coincident(g20,g21)
    c: Coincident(g21,g0)
FEATURE [PartDesign::Pad] Pad009
  Direction = (1,1,1)
  Length = 2.7
  Length2 = 100
  Placement = pos=(0,0,0) rot=(0.57735,0.57735,0.57735;2.0944rad)
  Profile = -> Sketch013
  Reversed = true
  Type = 0
FEATURE [PartDesign::Pad] Pad010
  BaseFeature = -> Pad009
  Direction = (1,1,1)
  Length = 6
  Length2 = 100
  Placement = pos=(0,0,0) rot=(0.57735,0.57735,0.57735;2.0944rad)
  Profile = -> Pad009 [Face24]
  Type = 0
FEATURE [Sketcher::SketchObject] Sketch014
  ExternalGeometry = -> [Pad010]
  FullyConstrained = false
  MapMode = 5
  Placement = pos=(1.08e-14,-1.43e-14,-16.1338) rot=(0.707107,0.707107,0;3.14159rad)
  Support = -> [Pad010]
  sketch-geometry (4):
    g0: LineSegment StartX=46.9706 StartY=2.7 StartZ=0 EndX=20.5608 EndY=2.7 EndZ=0
    g1: LineSegment StartX=20.5608 StartY=2.7 StartZ=0 EndX=20.5608 EndY=6 EndZ=0
    g2: LineSegment StartX=20.5608 StartY=6 StartZ=0 EndX=46.9706 EndY=6 EndZ=0
    g3: LineSegment StartX=46.9706 StartY=6 StartZ=0 EndX=46.9706 EndY=2.7 EndZ=0
  constraints (10):
    c: Coincident(g0,g1)
    c: Coincident(g1,g2)
    c: Coincident(g2,g3)
    c: Coincident(g3,g0)
    c: Horizontal(g0)
    c: Horizontal(g2)
    c: Vertical(g1)
    c: Vertical(g3)
    c: PointOnObject(g0,g-3)
    c: Distance(g1,g-4) = 2.7
FEATURE [PartDesign::Pocket] Pocket002
  BaseFeature = -> Pad010
  Length = 35
  Length2 = 100
  Midplane = true
  Placement = pos=(0,0,0) rot=(0.57735,0.57735,0.57735;2.0944rad)
  Profile = -> Sketch014
  Type = 0
FEATURE [PartDesign::Fillet] Fillet004
  Base = -> Pocket002 [Edge124]
  BaseFeature = -> Pocket002
  Placement = pos=(0,0,0) rot=(0.57735,0.57735,0.57735;2.0944rad)
  Radius = 15
  SupportTransform = false
FEATURE [PartDesign::Fillet] Fillet005
  Base = -> Fillet004 [Edge76]
  BaseFeature = -> Fillet004
  Placement = pos=(0,0,0) rot=(0.57735,0.57735,0.57735;2.0944rad)
  Radius = 4
  SupportTransform = false
FEATURE [PartDesign::Fillet] Fillet006
  Base = -> Fillet005 [Edge128]
  BaseFeature = -> Fillet005
  Placement = pos=(0,0,0) rot=(0.57735,0.57735,0.57735;2.0944rad)
  Radius = 6
  SupportTransform = false
FEATURE [Sketcher::SketchObject] Sketch015
  ExternalGeometry = -> [Fillet006]
  FullyConstrained = false
  MapMode = 5
  Placement = pos=(-3e-15,0.528911,3.2327) rot=(-0.080735,-0.080735,-0.993461;1.57736rad)
  Support = -> [Fillet006]
  sketch-geometry (4):
    g0: LineSegment StartX=-28.2685 StartY=8.7 StartZ=0 EndX=-19.2622 EndY=17.0329 EndZ=0
    g1: LineSegment StartX=-19.2622 StartY=17.0329 StartZ=0 EndX=-19.2622 EndY=-8.33289 EndZ=0
    g2: LineSegment StartX=-19.2622 StartY=-8.33289 StartZ=0 EndX=-28.2685 EndY=0 EndZ=0
    g3: LineSegment StartX=-28.2685 StartY=8.7 StartZ=0 EndX=-28.2685 EndY=0 EndZ=0
  constraints (8):
    c: PointOnObject(g0,g-3)
    c: Coincident(g0,g1)
    c: Vertical(g1)
    c: Coincident(g1,g2)
    c: PointOnObject(g2,g-4)
    c: Vertical(g2,g0)
    c: Equal(g0,g2)
    c: Coincident(g3,g0)
FEATURE [PartDesign::Body] Body005
  Group = -> [Sketch013,Pad009,Pad010,Sketch014,Pocket002,Fillet004,Fillet005,Fillet006,Sketch015]
  Origin = -> Origin011
  Placement = pos=(26.9,0,0) rot=(0,0,1;0rad)
  Tip = -> Fillet006
FEATURE [Part::MultiFuse] Fusion
  Shapes = -> [Body,Body001,Body002]
FEATURE [Part::Cylinder] Cylinder006  label="圆柱体006"
  Angle = 360
  AttacherType = Attacher::AttachEngine3D
  Height = 24
  Placement = pos=(20.3,6.5,-11.7) rot=(0,0,1;0rad)
  Radius = 3
FEATURE [Part::Cylinder] Cylinder007  label="圆柱体007"
  Angle = 360
  AttacherType = Attacher::AttachEngine3D
  Height = 24
  Placement = pos=(42.5,6.5,-11.7) rot=(0,0,1;0rad)
  Radius = 3
FEATURE [App::Part] Part006
  Group = -> [Cylinder006,Cylinder007]
  Origin = -> Origin012
FEATURE [Part::Cut] Cut003
  Base = -> Fusion
  Tool = -> Part006
FEATURE [App::MeasureDistance] Distance  label="Distance: 19.98 mm"
  Distance = 19.983
  P1 = (-10.369,-3.25069,0)
  P2 = (9.61406,-3.21754,0)
